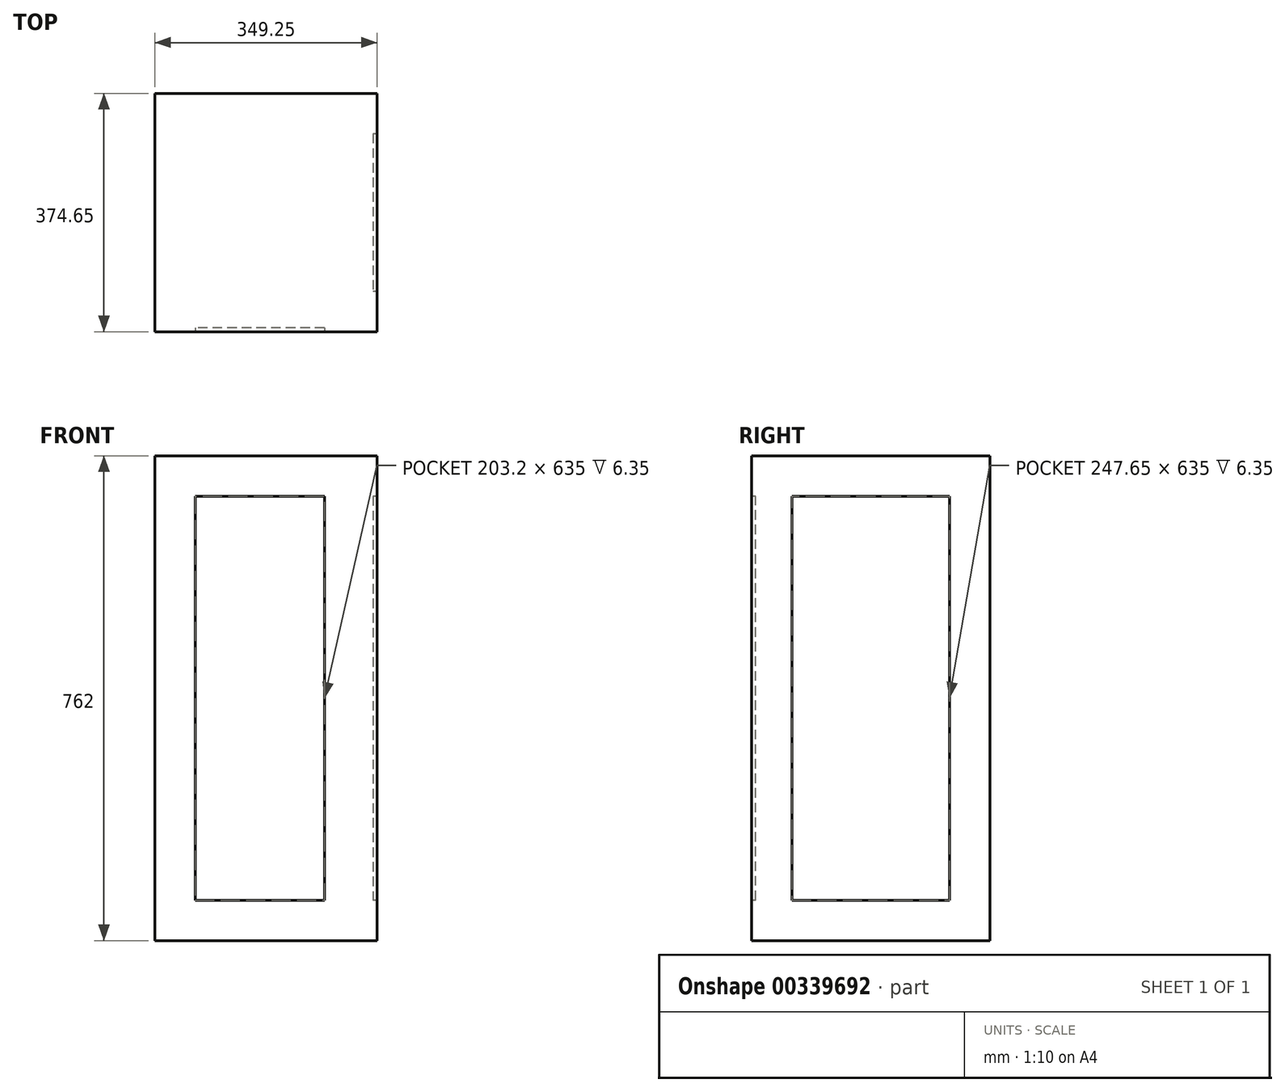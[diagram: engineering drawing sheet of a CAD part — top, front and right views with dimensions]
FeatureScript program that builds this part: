
annotation { "Feature Type Name" : "Feature", "Feature Type Description" : "" }
export const myFeature = defineFeature(function(context is Context, id is Id, definition is map)
    precondition{}
    {
        {
            var Q0;
            Q0=qCreatedBy(makeId("Front.planeOp"),FACE);
            var sketch = newSketch(context, id + "F0", { "sketchPlane" : qUnion([Q0])});
            skLineSegment(sketch, "E0.bottom", {"start": v(213.13, 0) * mm, "end": v(-117.07, 0) * mm});
            skLineSegment(sketch, "E0.top", {"start": v(213.13, 762) * mm, "end": v(-117.07, 762) * mm});
            skLineSegment(sketch, "E0.left", {"start": v(213.13, 0) * mm, "end": v(213.13, 762) * mm});
            skLineSegment(sketch, "E0.right", {"start": v(-117.07, 0) * mm, "end": v(-117.07, 762) * mm});
            skLineSegment(sketch, "E1.0", {"start": v(149.63, 698.5) * mm, "end": v(-53.57, 698.5) * mm});
            skLineSegment(sketch, "E1.1", {"start": v(149.63, 63.5) * mm, "end": v(149.63, 698.5) * mm});
            skLineSegment(sketch, "E1.2", {"start": v(149.63, 63.5) * mm, "end": v(-53.57, 63.5) * mm});
            skLineSegment(sketch, "E1.3", {"start": v(-53.57, 63.5) * mm, "end": v(-53.57, 698.5) * mm});
            skLineSegment(sketch, "E2.bottom", {"start": v(-117.07, 0) * mm, "end": v(263.93, 0) * mm});
            skLineSegment(sketch, "E3.bottom", {"start": v(-117.07, 762) * mm, "end": v(263.93, 762) * mm});
            skSolve(sketch);
        }
        {
            var Q0;
            Q0=makeQuery(id+"F0.imprint","IMPRINT",FACE,{"disambiguationData":[TD([[makeQuery(id+"F0.imprint","IMPRINT",EDGE,{"derivedFrom":sQuery(id+"F0.wireOp",EDGE,"E0.top")}),1.0]])]});
            var Q1;
            Q1=makeQuery(id+"F0.imprint","IMPRINT",FACE,{"disambiguationData":[TD([[makeQuery(id+"F0.imprint","IMPRINT",EDGE,{"derivedFrom":sQuery(id+"F0.wireOp",EDGE,"E1.0")}),1.0]])]});
            var Q2;
            Q2=makeQuery(id+"F0.imprint","IMPRINT",FACE,{"disambiguationData":[TD([[makeQuery(id+"F0.imprint","IMPRINT",EDGE,{"derivedFrom":sQuery(id+"F0.wireOp",EDGE,"E2.bottom")}),-1.0]])]});
            var Q3;
            Q3=makeQuery(id+"F0.imprint","IMPRINT",FACE,{"disambiguationData":[TD([[makeQuery(id+"F0.imprint","IMPRINT",EDGE,{"derivedFrom":sQuery(id+"F0.wireOp",EDGE,"E3.bottom")}),1.0]])]});
            var Q4;
            Q4=makeQuery(id+"F0.imprint","IMPRINT",FACE,{"disambiguationData":[TD([[makeQuery(id+"F0.imprint","IMPRINT",EDGE,{"derivedFrom":sQuery(id+"F0.wireOp",EDGE,"E0.left")}),1.0]])]});
            var Q5;
            Q5=makeQuery(id+"F0.imprint","IMPRINT",FACE,{"disambiguationData":[TD([[makeQuery(id+"F0.imprint","IMPRINT",EDGE,{"derivedFrom":sQuery(id+"F0.wireOp",EDGE,"E3.top")}),-1.0]])]});
            var Q6;
            Q6=makeQuery(id+"F0.imprint","IMPRINT",FACE,{"disambiguationData":[TD([[makeQuery(id+"F0.imprint","IMPRINT",EDGE,{"derivedFrom":sQuery(id+"F0.wireOp",EDGE,"E3.bottom")}),1.0]])]});
            extrude(context, id + "F1", {"entities" : qUnion([Q0, Q1, Q2, Q3, Q4, Q5, Q6]), "oppositeDirection" : true, "depth" : 374.65 * mm, "offsetDistance" : 25.4 * mm});
        }
        {
            var Q0;
            Q0=makeQuery(id+"F0.imprint","IMPRINT",FACE,{"disambiguationData":[TD([[makeQuery(id+"F0.imprint","IMPRINT",EDGE,{"derivedFrom":sQuery(id+"F0.wireOp",EDGE,"E1.0")}),1.0]])]});
            var Q1;
            Q1=makeQuery(id+"F0.imprint","IMPRINT",FACE,{"disambiguationData":[TD([[makeQuery(id+"F0.imprint","IMPRINT",EDGE,{"derivedFrom":sQuery(id+"F0.wireOp",EDGE,"E3.bottom")}),1.0]])]});
            extrude(context, id + "F2", {"entities" : qUnion([Q0, Q1]), "operationType" : NewBodyOperationType.REMOVE, "oppositeDirection" : true, "depth" : 6.35 * mm});
        }
        {
            var Q0;
            Q0=makeQuery(id+"F1.opExtrude","SWEPT_FACE",FACE,{"disambiguationData":[OSD([sQuery(id+"F0.wireOp",EDGE,"E0.left")])]});
            var sketch = newSketch(context, id + "F3", { "sketchPlane" : qUnion([Q0])});
            skLineSegment(sketch, "E4.bottom", {"start": v(374.65, 762) * mm, "end": v(0, 762) * mm});
            skLineSegment(sketch, "E4.top", {"start": v(374.65, 0) * mm, "end": v(0, 0) * mm});
            skLineSegment(sketch, "E4.left", {"start": v(374.65, 762) * mm, "end": v(374.65, 0) * mm});
            skLineSegment(sketch, "E4.right", {"start": v(0, 762) * mm, "end": v(0, 0) * mm});
            skLineSegment(sketch, "E5.0", {"start": v(311.15, 698.5) * mm, "end": v(63.5, 698.5) * mm});
            skLineSegment(sketch, "E5.1", {"start": v(311.15, 698.5) * mm, "end": v(311.15, 63.5) * mm});
            skLineSegment(sketch, "E5.2", {"start": v(311.15, 63.5) * mm, "end": v(63.5, 63.5) * mm});
            skLineSegment(sketch, "E5.3", {"start": v(63.5, 698.5) * mm, "end": v(63.5, 63.5) * mm});
            skSolve(sketch);
        }
        {
            var Q0;
            Q0 = qSketchRegion(id + "F3", true);
            extrude(context, id + "F4", {"entities" : qUnion([Q0]), "operationType" : NewBodyOperationType.ADD, "depth" : 19.05 * mm, "offsetDistance" : 25.4 * mm});
        }
        {
            var Q0;
            Q0=makeQuery(id+"F1.opExtrude","SWEPT_FACE",FACE,{"disambiguationData":[OSD([sQuery(id+"F0.wireOp",EDGE,"E0.left")])]});
            extrude(context, id + "F5", {"entities" : qUnion([Q0]), "operationType" : NewBodyOperationType.ADD, "depth" : 12.7 * mm, "offsetDistance" : 25.4 * mm});
        }
    });
